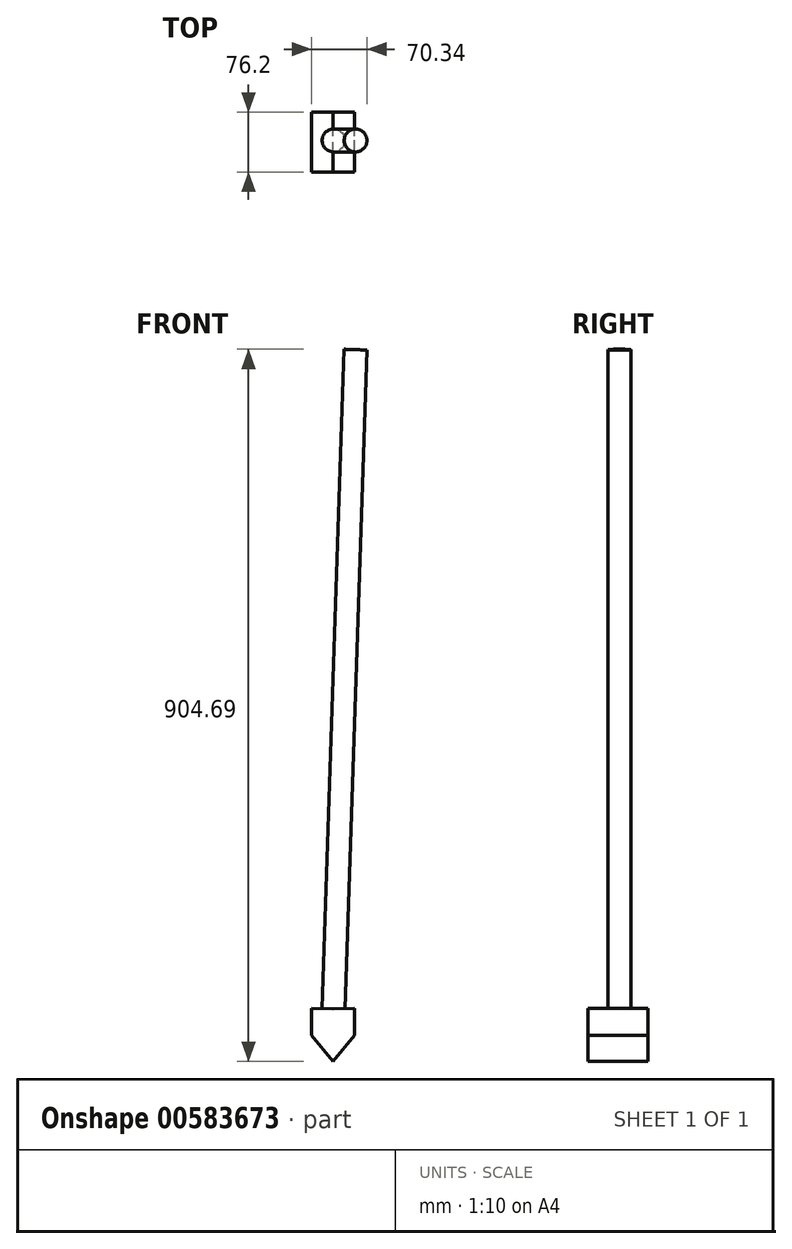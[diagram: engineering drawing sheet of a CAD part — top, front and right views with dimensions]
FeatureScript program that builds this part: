
annotation { "Feature Type Name" : "Feature", "Feature Type Description" : "" }
export const myFeature = defineFeature(function(context is Context, id is Id, definition is map)
    precondition{}
    {
        {
            var Q0;
            Q0=qCreatedBy(makeId("Front.planeOp"),FACE);
            var sketch = newSketch(context, id + "F0", { "sketchPlane" : qUnion([Q0])});
            skLineSegment(sketch, "E0", {"start": v(0, 0) * mm, "end": v(-27.23, 32.95) * mm});
            skLineSegment(sketch, "E1", {"start": v(-27.23, 32.95) * mm, "end": v(-27.23, 67.4) * mm});
            skLineSegment(sketch, "E2", {"start": v(0, 66.5) * mm, "end": v(0, 66.5) * mm});
            skLineSegment(sketch, "E3", {"start": v(0, 93.94) * mm, "end": v(0, 93.94) * mm});
            skLineSegment(sketch, "E4", {"start": v(-27.23, 67.4) * mm, "end": v(0, 66.5) * mm});
            skLineSegment(sketch, "E5", {"start": v(0, 0) * mm, "end": v(0, 66.5) * mm});
            skLineSegment(sketch, "E6.MirrorCS", {"start": v(0, 0) * mm, "end": v(27.23, 32.95) * mm});
            skLineSegment(sketch, "E7.MirrorCS", {"start": v(27.23, 32.95) * mm, "end": v(27.23, 67.4) * mm});
            skLineSegment(sketch, "E8.MirrorCS", {"start": v(27.23, 67.4) * mm, "end": v(0, 66.5) * mm});
            skSolve(sketch);
        }
        {
            var Q0;
            Q0=makeQuery(id+"F0.imprint","IMPRINT",FACE,{"disambiguationData":[TD([[makeQuery(id+"F0.imprint","IMPRINT",EDGE,{"derivedFrom":sQuery(id+"F0.wireOp",EDGE,"E5")}),-1.0]])]});
            var Q1;
            Q1=makeQuery(id+"F0.imprint","IMPRINT",FACE,{"disambiguationData":[TD([[makeQuery(id+"F0.imprint","IMPRINT",EDGE,{"derivedFrom":sQuery(id+"F0.wireOp",EDGE,"E0")}),-1.0]])]});
            extrude(context, id + "F1", {"entities" : qUnion([Q0, Q1]), "depth" : 76.2 * mm, "offsetDistance" : 25.4 * mm});
        }
        {
            var Q0;
            Q0=makeQuery(id+"F1.opExtrude","SWEPT_FACE",FACE,{"disambiguationData":[OSD([sQuery(id+"F0.wireOp",EDGE,"E4")])]});
            var sketch = newSketch(context, id + "F2", { "sketchPlane" : qUnion([Q0])});
            skCircle(sketch, "E9", {"center": v(-1.58, -35.97) * mm, "radius": 14.52 * mm});
            skSolve(sketch);
        }
        {
            var Q0;
            Q0 = qSketchRegion(id + "F2", true);
            extrude(context, id + "F3", {"entities" : qUnion([Q0]), "operationType" : NewBodyOperationType.ADD, "depth" : 838.2 * mm, "offsetDistance" : 25.4 * mm});
        }
    });
